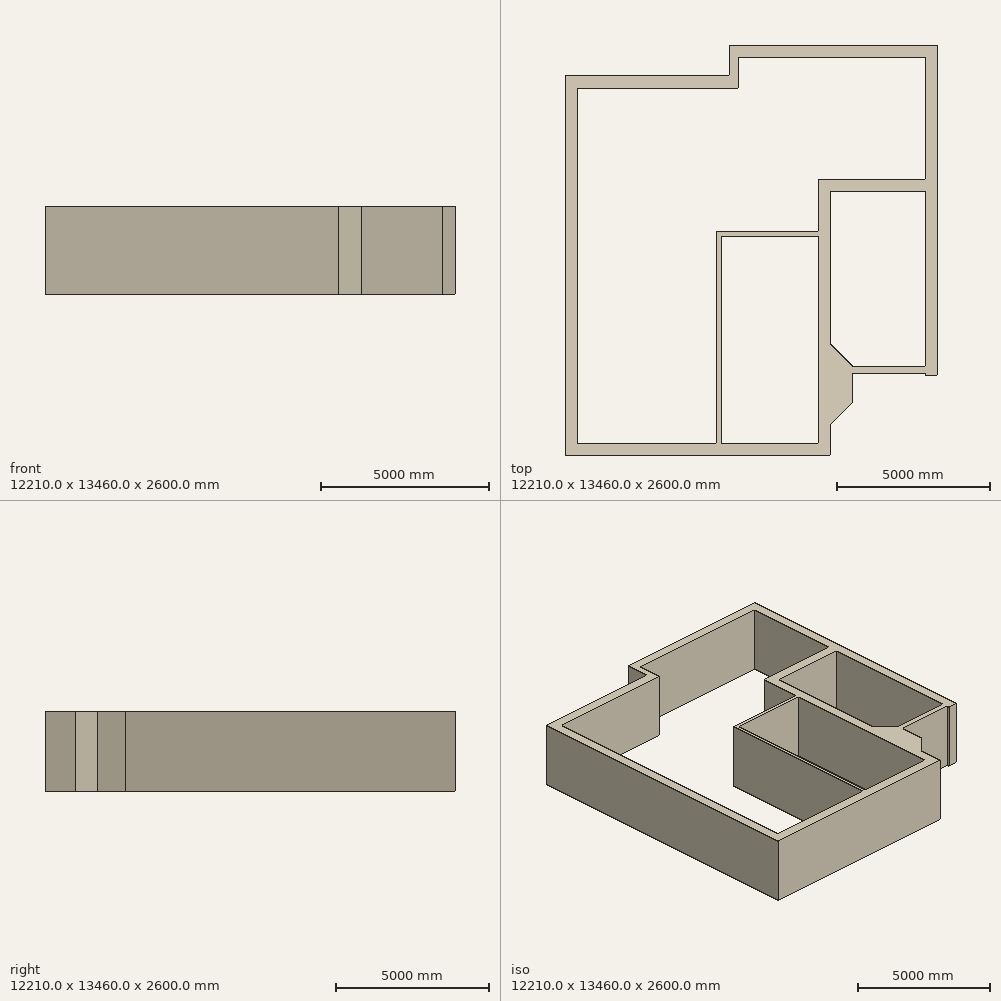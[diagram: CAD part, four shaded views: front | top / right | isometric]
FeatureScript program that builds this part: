
annotation { "Feature Type Name" : "Feature", "Feature Type Description" : "" }
export const myFeature = defineFeature(function(context is Context, id is Id, definition is map)
    precondition{}
    {
        {
            var Q0;
            Q0=qCreatedBy(makeId("Top.planeOp"),FACE);
            var sketch = newSketch(context, id + "F0", { "sketchPlane" : qUnion([Q0])});
            skSolve(sketch);
        }
        {
            var Q0;
            Q0=qCreatedBy(makeId("Top.planeOp"),FACE);
            var sketch = newSketch(context, id + "F1", { "sketchPlane" : qUnion([Q0])});
            skLineSegment(sketch, "E0.bottom", {"start": v(-6326.7, -10454.97) * mm, "end": v(2383.3, -10454.97) * mm});
            skLineSegment(sketch, "E0.top", {"start": v(-6326.7, 2005.03) * mm, "end": v(-936.7, 2005.03) * mm});
            skLineSegment(sketch, "E0.left", {"start": v(-6326.7, -10454.97) * mm, "end": v(-6326.7, 2005.03) * mm});
            skLineSegment(sketch, "E0.right", {"start": v(2383.3, -10454.97) * mm, "end": v(2383.3, -9454.97) * mm});
            skLineSegment(sketch, "E1.bottom", {"start": v(5883.3, 3005.03) * mm, "end": v(-936.7, 3005.03) * mm});
            skLineSegment(sketch, "E1.top", {"start": v(5883.3, -1794.97) * mm, "end": v(2383.3, -1794.97) * mm});
            skLineSegment(sketch, "E1.left", {"start": v(5883.3, 3005.03) * mm, "end": v(5883.3, -1794.97) * mm});
            skLineSegment(sketch, "E1.right", {"start": v(-936.7, 3005.03) * mm, "end": v(-936.7, 2005.03) * mm});
            skLineSegment(sketch, "E2.bottom", {"start": v(5883.3, -7834.97) * mm, "end": v(5483.3, -7834.97) * mm});
            skLineSegment(sketch, "E2.top", {"start": v(5883.3, -1794.97) * mm, "end": v(5483.3, -1794.97) * mm});
            skLineSegment(sketch, "E2.left", {"start": v(5883.3, -7834.97) * mm, "end": v(5883.3, -1794.97) * mm});
            skLineSegment(sketch, "E2.right", {"start": v(5483.3, -7834.97) * mm, "end": v(5483.3, -7747.86) * mm});
            skLineSegment(sketch, "E3.bottom", {"start": v(-5926.7, 1605.03) * mm, "end": v(-647.47, 1605.03) * mm});
            skLineSegment(sketch, "E3.top", {"start": v(-5926.7, -10054.97) * mm, "end": v(-1366.7, -10054.97) * mm});
            skLineSegment(sketch, "E3.left", {"start": v(-5926.7, 1605.03) * mm, "end": v(-5926.7, -10054.97) * mm});
            skLineSegment(sketch, "E3.right", {"start": v(1983.3, -1394.97) * mm, "end": v(1983.3, -3104.97) * mm});
            skLineSegment(sketch, "E4.bottom", {"start": v(5483.3, 2605.03) * mm, "end": v(-647.47, 2605.03) * mm});
            skLineSegment(sketch, "E4.top", {"start": v(5483.3, -1394.97) * mm, "end": v(1983.3, -1394.97) * mm});
            skLineSegment(sketch, "E4.left", {"start": v(5483.3, 2605.03) * mm, "end": v(5483.3, -1394.97) * mm});
            skLineSegment(sketch, "E4.right", {"start": v(-647.47, 2605.03) * mm, "end": v(-647.47, 1605.03) * mm});
            skLineSegment(sketch, "E5", {"start": v(2383.3, -6814.18) * mm, "end": v(3090.4, -7521.3) * mm});
            skLineSegment(sketch, "E6", {"start": v(3090.4, -7521.3) * mm, "end": v(5483.3, -7521.3) * mm});
            skLineSegment(sketch, "E7", {"start": v(2383.3, -9454.97) * mm, "end": v(3090.4, -8747.86) * mm});
            skLineSegment(sketch, "E8", {"start": v(3090.4, -8747.86) * mm, "end": v(3090.4, -7747.86) * mm});
            skLineSegment(sketch, "E9", {"start": v(3090.4, -7747.86) * mm, "end": v(5483.3, -7747.86) * mm});
            skLineSegment(sketch, "E10.trimOffspring", {"start": v(2383.3, -6814.18) * mm, "end": v(2383.3, -1794.97) * mm});
            skLineSegment(sketch, "E11.trimOffspring", {"start": v(5483.3, -7521.3) * mm, "end": v(5483.3, -1794.97) * mm});
            skLineSegment(sketch, "E12", {"start": v(1983.3, -3104.97) * mm, "end": v(-1366.7, -3104.97) * mm});
            skLineSegment(sketch, "E13", {"start": v(-1366.7, -3104.97) * mm, "end": v(-1366.7, -10054.97) * mm});
            skLineSegment(sketch, "E14", {"start": v(-1216.7, -10054.97) * mm, "end": v(-1216.7, -3254.97) * mm});
            skLineSegment(sketch, "E15", {"start": v(-1216.7, -3254.97) * mm, "end": v(1983.3, -3254.97) * mm});
            skLineSegment(sketch, "E16.trimOffspring", {"start": v(-1216.7, -10054.97) * mm, "end": v(1983.3, -10054.97) * mm});
            skLineSegment(sketch, "E17.trimOffspring", {"start": v(1983.3, -3254.97) * mm, "end": v(1983.3, -10054.97) * mm});
            skSolve(sketch);
        }
        {
            var Q0;
            Q0=qSketchRegion(id+"F1",true);
            extrude(context, id + "F2", {"entities" : qUnion([Q0]), "depth" : 2600 * mm, "offsetDistance" : 25 * mm});
        }
    });
